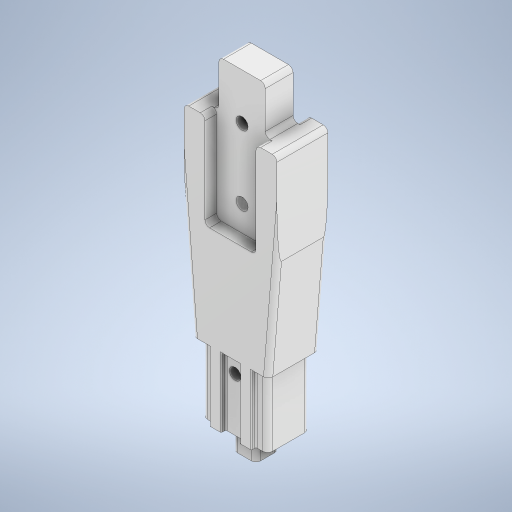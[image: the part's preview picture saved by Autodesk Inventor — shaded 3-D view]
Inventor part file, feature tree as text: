
AUTODESK INVENTOR PART (.ipt)
format: ipt  version: 2024.3 (Build 283343000, 343)  size: 551,936 bytes
history: native  units: mm
features: extrude x10, sketch x10, fillet x3, other x1, projected_geometry x1
ambient origin geometry x8: Origin, YZ Plane, XZ Plane, XY Plane, X Axis, Y Axis, Z Axis, Center Point
bodies: Body1 (feature_tree)
feature tree (25):
  other  "ソリッド1"
  extrude  "押し出し1"  Depth=40.0mm
  extrude  "押し出し2"  Depth=10.0mm
  extrude  "押し出し3"  Depth=10.0mm
  fillet  "フィレット1"  Radius=50.0mm
  extrude  "押し出し14"  Depth=10.0mm
  extrude  "押し出し15"  Depth=30.0mm
  extrude  "押し出し16"  Depth=5.2mm
  extrude  "押し出し18"  Depth=5.2mm
  extrude  "押し出し19"  Depth=20.0mm
  fillet  "フィレット5"  Radius=22.0mm
  extrude  "押し出し20"  Depth=120.0mm
  extrude  "押し出し21"  Depth=20.0mm
  fillet  "フィレット6"  Radius=50.0mm
  sketch  "スケッチ1"
  sketch  "スケッチ2"
  sketch  "スケッチ3"
  sketch  "スケッチ17"
  sketch  "スケッチ18"
  projected_geometry  "投影ループ3"
  sketch  "スケッチ19"
  sketch  "スケッチ21"
  sketch  "スケッチ22"
  sketch  "スケッチ23"
  sketch  "スケッチ24"
